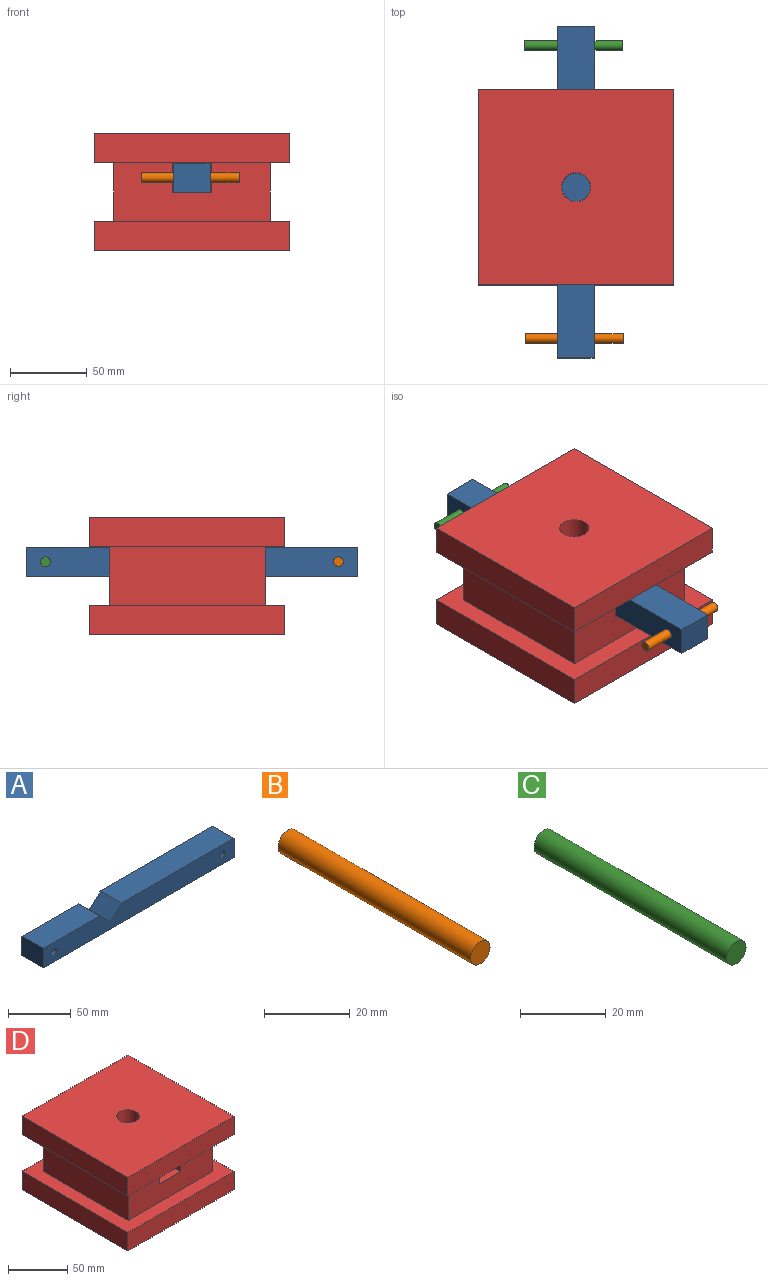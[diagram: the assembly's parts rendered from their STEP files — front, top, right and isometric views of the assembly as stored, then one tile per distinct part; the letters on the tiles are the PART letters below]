
ASSEMBLY  parts=4 mates=3
PART A: 11 faces, bbox 215.9x23.8x19.1 mm
  f0: plane 23.81x12.88mm, normal (-0.68,0,0.73), area 419.4mm2, adj f1,f6,f7,f8
  f1: plane 23.81x12.52mm, normal (0.69,0,0.72), area 413.3mm2, adj f0,f2,f7,f8
  f2: plane 63.5x23.81mm, normal (0,0,1), area 1512.1mm2, adj f1,f3,f7,f8
  f3: plane 23.81x19.05mm, normal (-1,0,0), area 453.6mm2, adj f2,f4,f7,f8
  f4: plane 215.9x23.81mm, normal (0,0,-1), area 5141.1mm2, adj f3,f5,f7,f8
  f5: plane 23.81x19.05mm, normal (1,0,0), area 453.6mm2, adj f4,f6,f7,f8
  f6: plane 127x23.81mm, normal (0,0,1), area 3024.2mm2, adj f0,f5,f7,f8
  f7: plane 215.9x19.05mm, normal (0,-1,0), area 3896.9mm2, adj f0,f1,f2,f3,f4,f5,f6,f9
  f8: plane 215.9x19.05mm, normal (0,1,0), area 3896.9mm2, adj f0,f1,f2,f3,f4,f5,f6,f9
  f9: cylinder r=3.17mm len=23.81mm, axis (0,-1,0), area 475mm2, adj f7,f8
  f10: cylinder r=3.17mm len=23.81mm, axis (0,-1,0), area 475mm2, adj f7,f8
PART B: 3 faces, bbox 6.4x63.5x6.4 mm
  f0: cylinder r=3.17mm len=63.5mm, axis (0,1,0), area 1266.8mm2, adj f1,f2
  f1: plane 6.35x6.35mm, normal (0,-1,0), area 31.7mm2, adj f0
  f2: plane 6.35x6.35mm, normal (0,1,0), area 31.7mm2, adj f0
PART C: 3 faces, bbox 6.4x63.5x6.4 mm
  f0: cylinder r=3.17mm len=63.5mm, axis (0,1,0), area 1266.8mm2, adj f1,f2
  f1: plane 6.35x6.35mm, normal (0,-1,0), area 31.7mm2, adj f0
  f2: plane 6.35x6.35mm, normal (0,1,0), area 31.7mm2, adj f0
PART D: 22 faces, bbox 127x127x76.2 mm
  f0: plane 101.6x38.1mm, normal (-1,0,0), area 3871mm2, adj f2,f3,f4,f10
  f1: plane 101.6x38.1mm, normal (1,0,0), area 3871mm2, adj f2,f3,f4,f10
  f2: plane 101.6x38.1mm, normal (0,1,0), area 3387.1mm2, adj f0,f1,f4,f10,f16,f17,f18,f19
  f3: plane 101.6x38.1mm, normal (0,-1,0), area 3387.1mm2, adj f0,f1,f4,f10,f16,f17,f18,f19
  f4: plane 127x127mm, normal (0,0,1), area 5806.4mm2, adj f0,f1,f2,f3,f5,f7,f8,f9
  f5: plane 127x19.05mm, normal (-1,0,0), area 2419.3mm2, adj f4,f6,f8,f9
  f6: plane 127x127mm, normal (0,0,-1), area 16129mm2, adj f5,f7,f8,f9
  f7: plane 127x19.05mm, normal (1,0,0), area 2419.3mm2, adj f4,f6,f8,f9
  f8: plane 127x19.05mm, normal (0,1,0), area 2419.3mm2, adj f4,f5,f6,f7
  f9: plane 127x19.05mm, normal (0,-1,0), area 2419.3mm2, adj f4,f5,f6,f7
  f10: plane 127x127mm, normal (0,0,-1), area 5806.4mm2, adj f0,f1,f2,f3,f11,f13,f14,f15
  f11: plane 127x19.05mm, normal (1,0,0), area 2419.3mm2, adj f10,f12,f14,f15
  f12: plane 127x127mm, normal (0,0,1), area 15844mm2, adj f11,f13,f14,f15,f21
  f13: plane 127x19.05mm, normal (-1,0,0), area 2419.3mm2, adj f10,f12,f14,f15
  f14: plane 127x19.05mm, normal (0,1,0), area 2419.4mm2, adj f10,f11,f12,f13
  f15: plane 127x19.05mm, normal (0,-1,0), area 2419.4mm2, adj f10,f11,f12,f13
  f16: plane 101.6x19.05mm, normal (-1,0,0), area 1935.5mm2, adj f2,f3,f17,f19
  f17: plane 101.6x25.4mm, normal (0,0,-1), area 2315.9mm2, adj f2,f3,f16,f18,f20
  f18: plane 101.6x19.05mm, normal (1,0,0), area 1935.5mm2, adj f2,f3,f17,f19
  f19: plane 101.6x25.4mm, normal (0,0,1), area 2580.6mm2, adj f2,f3,f16,f18
  f20: cone r=0mm half-angle=59deg, axis (0,0,1), area 23.7mm2, adj f17,f21
  f21: cylinder r=9.53mm len=19.05mm, axis (0,0,1), area 1140.1mm2, adj f12,f20
PLACE A rot(axis=(0,0,-1),90deg) t=(75.24,-60.17,78.91)mm
PLACE B rot(axis=(0.58,0.58,-0.58),120deg) t=(94.11,-80.41,69.38)mm
PLACE C rot(axis=(-0.58,-0.58,-0.58),120deg) t=(93.53,176.49,5.95)mm
PLACE D at identity fixed
MATE slider A.f3 <-> D.f2  axis (0,1,0) through (51.43,155.73,37.89)mm
MATE slider C.f0 <-> A.f9  axis (1,0,0) through (93.53,143.03,47.42)mm
MATE slider B.f0 <-> A.f10  axis (-1,0,0) through (30.61,-47.47,47.42)mm
